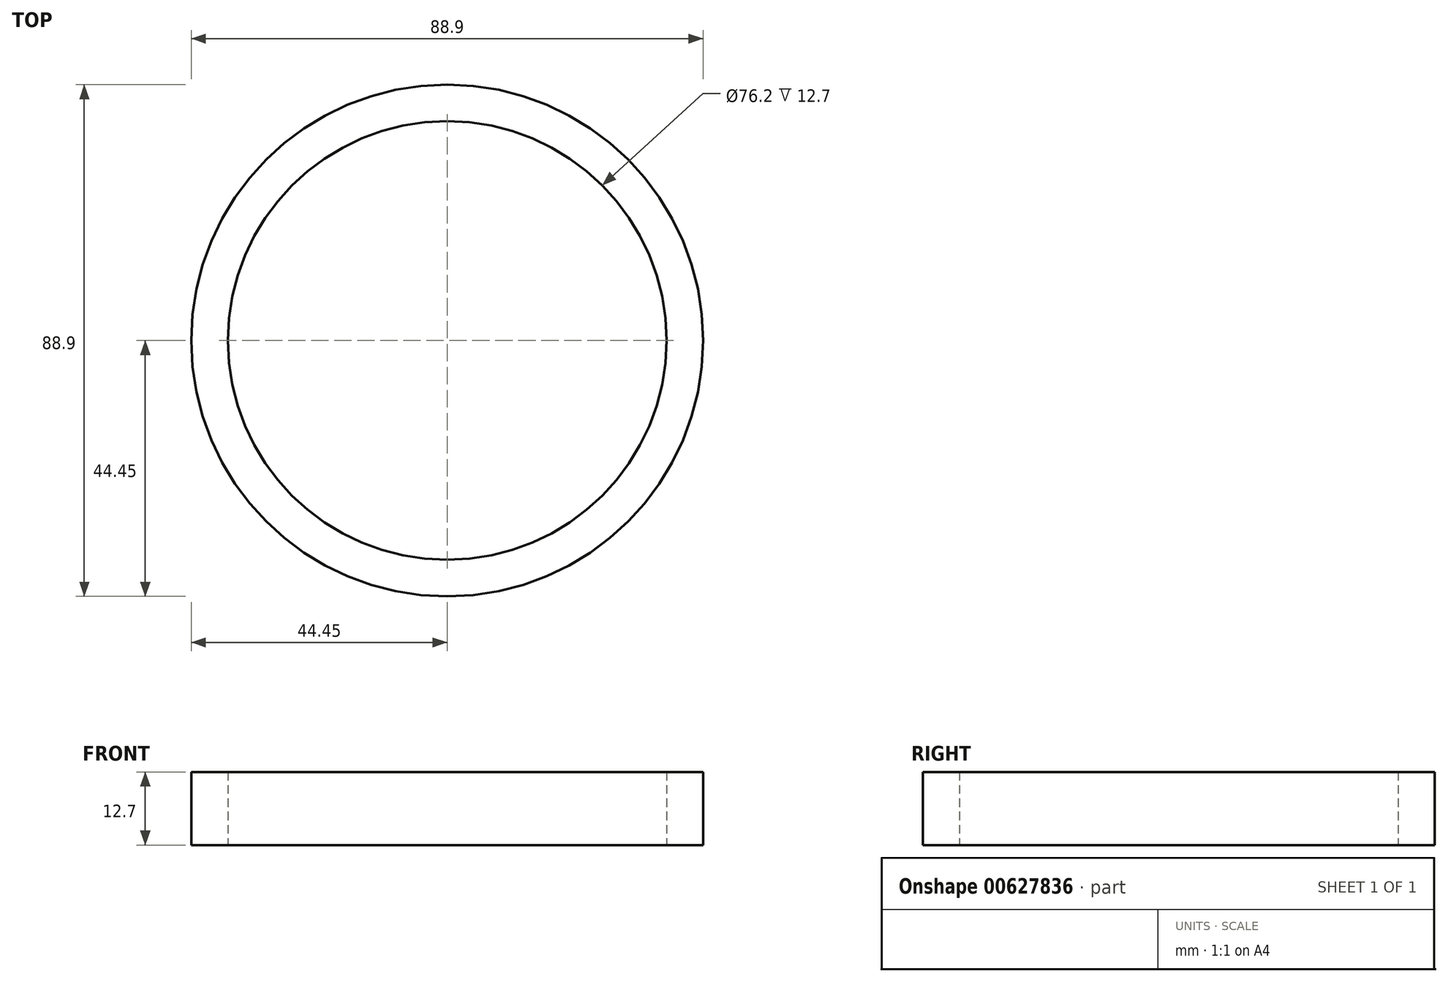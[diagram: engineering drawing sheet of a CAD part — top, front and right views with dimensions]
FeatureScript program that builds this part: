
annotation { "Feature Type Name" : "Feature", "Feature Type Description" : "" }
export const myFeature = defineFeature(function(context is Context, id is Id, definition is map)
    precondition{}
    {
        {
            var Q0;
            Q0=qCreatedBy(makeId("Top.planeOp"),FACE);
            var sketch = newSketch(context, id + "F0", { "sketchPlane" : qUnion([Q0])});
            skCircle(sketch, "E0", {"center": v(0, 0) * mm, "radius": 44.45 * mm});
            skCircle(sketch, "E1", {"center": v(0, 0) * mm, "radius": 38.1 * mm});
            skSolve(sketch);
        }
        {
            var Q0;
            Q0=makeQuery(id+"F0.imprint","IMPRINT",FACE,{"disambiguationData":[TD([[makeQuery(id+"F0.imprint","IMPRINT",EDGE,{"derivedFrom":sQuery(id+"F0.wireOp",EDGE,"E0")}),1.0]])]});
            extrude(context, id + "F1", {"entities" : qUnion([Q0]), "depth" : 12.7 * mm, "offsetDistance" : 25.4 * mm});
        }
    });
